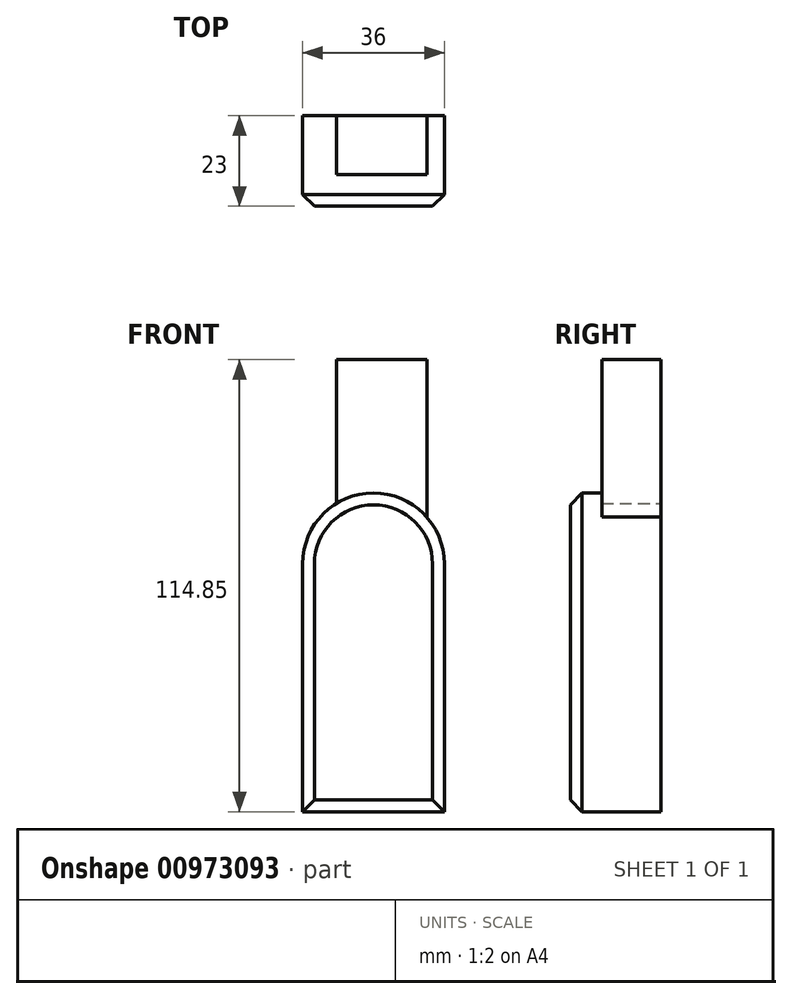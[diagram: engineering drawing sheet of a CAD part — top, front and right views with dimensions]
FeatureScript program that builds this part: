
annotation { "Feature Type Name" : "Feature", "Feature Type Description" : "" }
export const myFeature = defineFeature(function(context is Context, id is Id, definition is map)
    precondition{}
    {
        {
            var Q0;
            Q0=qCreatedBy(makeId("Front.planeOp"),FACE);
            var sketch = newSketch(context, id + "F0", { "sketchPlane" : qUnion([Q0])});
            skLineSegment(sketch, "E0.bottom", {"start": v(0, 0) * mm, "end": v(36, 0) * mm});
            skLineSegment(sketch, "E0.top", {"start": v(0, 63) * mm, "end": v(36, 63) * mm});
            skLineSegment(sketch, "E0.left", {"start": v(0, 0) * mm, "end": v(0, 63) * mm});
            skLineSegment(sketch, "E0.right", {"start": v(36, 0) * mm, "end": v(36, 63) * mm});
            skArc(sketch, "E1", {"start": v(36, 63) * mm, "mid": v(18, 81) * mm, "end": v(0, 63) * mm});
            skSolve(sketch);
        }
        {
            var Q0;
            Q0=makeQuery(id+"F0.imprint","IMPRINT",FACE,{"disambiguationData":[TD([[makeQuery(id+"F0.imprint","IMPRINT",EDGE,{"derivedFrom":sQuery(id+"F0.wireOp",EDGE,"E0.top")}),1.0]])]});
            var Q1;
            Q1=makeQuery(id+"F0.imprint","IMPRINT",FACE,{"disambiguationData":[TD([[makeQuery(id+"F0.imprint","IMPRINT",EDGE,{"derivedFrom":sQuery(id+"F0.wireOp",EDGE,"E0.bottom")}),1.0]])]});
            extrude(context, id + "F1", {"entities" : qUnion([Q0, Q1]), "depth" : 23 * mm, "offsetDistance" : 25 * mm});
        }
        {
            var Q0;
            Q0=makeQuery(id+"F1.opExtrude","CAP_FACE",FACE,{"disambiguationData":[OSD([sQuery(id+"F0.wireOp",EDGE,"E0.bottom"),sQuery(id+"F0.wireOp",EDGE,"E0.left"),sQuery(id+"F0.wireOp",EDGE,"E0.right"),sQuery(id+"F0.wireOp",EDGE,"E1")])],"isStart":false});
            chamfer(context, id + "F2", {"entities" : qUnion([Q0]), "width" : 3 * mm, "tangentPropagation" : true});
        }
        {
            var Q0;
            Q0=qCreatedBy(makeId("Front.planeOp"),FACE);
            var sketch = newSketch(context, id + "F3", { "sketchPlane" : qUnion([Q0])});
            skLineSegment(sketch, "E2.bottom", {"start": v(10.28, 79.26) * mm, "end": v(9.14, 79.26) * mm});
            skPoint(sketch, "E3.orphan", {"position": v(0, 63) * mm});
            skPoint(sketch, "E4.0.end.orphan", {"position": v(36, 63) * mm});
            skArc(sketch, "E5.0", {"start": v(0, 63) * mm, "mid": v(18, 81) * mm, "end": v(36, 63) * mm});
            skLineSegment(sketch, "E6.bottom", {"start": v(31.55, 74.85) * mm, "end": v(8.55, 74.85) * mm});
            skLineSegment(sketch, "E6.top", {"start": v(31.55, 114.85) * mm, "end": v(8.55, 114.85) * mm});
            skLineSegment(sketch, "E6.left", {"start": v(31.55, 74.85) * mm, "end": v(31.55, 114.85) * mm});
            skLineSegment(sketch, "E6.right", {"start": v(8.55, 74.85) * mm, "end": v(8.55, 114.85) * mm});
            skSolve(sketch);
        }
        {
            var Q0;
            Q0 = qSketchRegion(id + "F3", true);
            extrude(context, id + "F4", {"entities" : qUnion([Q0]), "operationType" : NewBodyOperationType.ADD, "depth" : 15 * mm, "offsetDistance" : 25 * mm});
        }
    });
